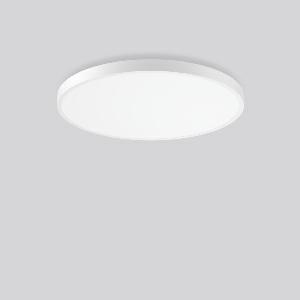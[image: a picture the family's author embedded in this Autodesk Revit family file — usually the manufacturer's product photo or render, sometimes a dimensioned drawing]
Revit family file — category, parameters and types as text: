
# Revit family: triona_round_a_312387_002_1_76_3ab7
name_source: partatom
category: Lighting Fixtures
units: mm (PartAtom-declared; Revit-internal decimal feet)

## family parameters
Cut with Voids When Loaded = No
Host = Face
Light Source = No
Part Type = Normal
Room Calculation Point = No
Round Connector Dimension = Use Diameter
Shared = No

## types (1)
- TRIONA round A (1 x LED Modul 840, 8300 lm, 4000)
    Apparent Load = 80 VA
    CIE Flux Codes = 49 80 96 100 100
    Color Rendering = 80
    Color Temperature = 4000
    Default Elevation = 1800 mm
    Description = Series: TRIONA round
Decorative round LED surface-mounted luminaire. Flat, seamless frame: aluminium extrusion profile, powder coated. Cover made of sheet steel, powder-coated. Light emission through a diffuser: plastic, opal. Lightguide and diffuser made of non-yellowing plastic (PMMA). Lateral light emission (RZB SIDELITE technology) for above-average homogeneous light distribution. Suitable for Ceiling mounting, Wall (surface). Tool-free mounting via bayonet connection. Electronic ballast included. Very easy installation thanks to Plug+Play connection. 
Colour: traffic white, matt (RAL 9016)
Diameter: 845 mm
Height: 88 mm
Lamp: LED
Socket: without socket
Colour temperature: 4000K
Colour rendering index (CRI): 80
System power: 80 W
Rated luminous flux: 8300 lm
Luminous efficiency: 104 lm/W
Control gear: Converter, dimmable, DALI
Protection class: I
Type of protection: IP 20
    Height = 88 mm
    Lamp = 1 x LED Modul 840
    Lamp Light Flux = 8300 lm
    Lamp count = 1
    Length = 845 mm
    Lifetime = 50000 h
    Luminous efficacy = 104 lm/W
    Manufacturer = RZB
    ModVariant = No
    Model = 312387.002.1.76
    Mounting Place = Ceiling
    Mounting Type = Surface mounted
    Number of Poles = 1
    OnlyDefault = Yes
    Power Factor = 1
    Product Name = TRIONA round A
    Product group = Surface mounted modular luminaires
    ProductGroupID = 306
    Protection Class = Protection class I
    Protection Degree = IP 20
    RLX_Detail_Level = 1
    RLX_Emergency_Light_Flux = 0 lm
    RLX_Emergency_Type = 0
    RLX_Emergency_Type_DB = No
    RlxData = <blob elided: 32357 chars, md5=05505e06>
    Socket = socket
    Standby Power = 0 W
    System Light Flux = 8300 lm
    System Power = 80 W
    Type Comments = Product without accessories
    Type Image = 312388.002.jpg
    URL = http://relux.com
    VarID = ---
    Voltage = 230 V
    Voltage Range = 220-240 V
    Weight = 0.00 kg
    Width = 0 mm  [stored 0 ft]

note: [stored X ft] marks values corroborated as IEEE doubles in the binary element streams (Revit-internal decimal feet)

## geometry (parser evidence)
native form markers: Blend x4, Sweep x11
no freeform markers — native parametric forms only
